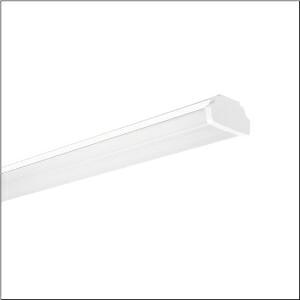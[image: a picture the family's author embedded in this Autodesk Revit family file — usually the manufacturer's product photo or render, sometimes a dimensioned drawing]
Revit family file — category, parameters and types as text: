
# Revit family: modario_r__31_mo_53bm812d2v6085_42f2
name_source: partatom
category: Lighting Fixtures
units: mm (PartAtom-declared; Revit-internal decimal feet)

## family parameters
Cut with Voids When Loaded = No
Host = Face
Light Source = No
Part Type = Normal
Room Calculation Point = No
Round Connector Dimension = Use Diameter
Shared = No

## types (1)
- --- (1 x LED, 8960 lm, 61.8 W, 6500K)
    Apparent Load = 62 VA
    CIE Flux Codes = 47 80 95 92 100
    Color Rendering = 80
    Color Temperature = 6500K
    Default Elevation = 1800 mm
    Description = Modario® 31 MO, luminaire insert, of sheet steel, coil coated, white, length: 1.495mm, width: 81mm, height: 82mm, 5x system unit, system units: 299mm, LED rated luminous flux: 8.960lm, light colour: 865, control gear: DALI 2, control gear: ECG DALI, with plug, 5-pole, with phase selection, mains connection: 220..240V, AC, 50/60Hz, rated input power: 62W, through-wiring accessed according to module size, primary optical cover: cover, of PMMA, light emission: direct distribution, primary light characteristic: symmetric, protection rating (complete): IP20, protection rating (LED compartment): IP50, insulation class (complete): insulation class I (protective earthing), certification: CE, ENEC, VDE, UKCA, impact resistance: IK03, permissible ambient temperature for indoor applications: -25..+30°C, corresponds to IFS (International Featured Standards) requirements for safety and quality in the food industry, reducing of maximum allowable ambient temperature of 5°C with ceiling mounting, packaging unit: 1 piece
    Height = 92 mm
    Lamp = 1 x LED
    Lamp Light Flux = 8960 lm
    Lamp Power = 61.8 W
    Lamp count = 1
    Length = 1495 mm
    Luminous efficacy = 145 lm/W
    Manufacturer = Siteco
    ModVariant = No
    Model = 53BM812D2V6085
    Mounting Place = Ceiling
    Mounting Type = Pendant
    Number of Poles = 1
    OnlyDefault = Yes
    Power Factor = 1
    Product Name = Modario® 31 MO
    Product group = luminaire insert
    ProductGroupID = 901
    Protection Class = Protection class I
    Protection Degree = IP 20
    RLX_Detail_Level = 1
    RLX_Emergency_Light_Flux = 0 lm
    RLX_Emergency_Type = 0
    RLX_Emergency_Type_DB = No
    RlxData = <blob elided: 42261 chars, md5=3bc84d04>
    Socket = socket
    Standby Power = 0 W
    System Light Flux = 8960 lm
    System Power = 62 W
    Type Comments = factory setting: luminous flux: 100 % | dim-lin: 254 | 500 mA
    Type Image = l_1300283.jpg
    URL = http://relux.com
    VarID = @adj_130737
    Voltage = 0 V
    Weight = 0.00 kg
    Width = 81 mm

## geometry (parser evidence)
native form markers: Blend x4, Sweep x11
no freeform markers — native parametric forms only
